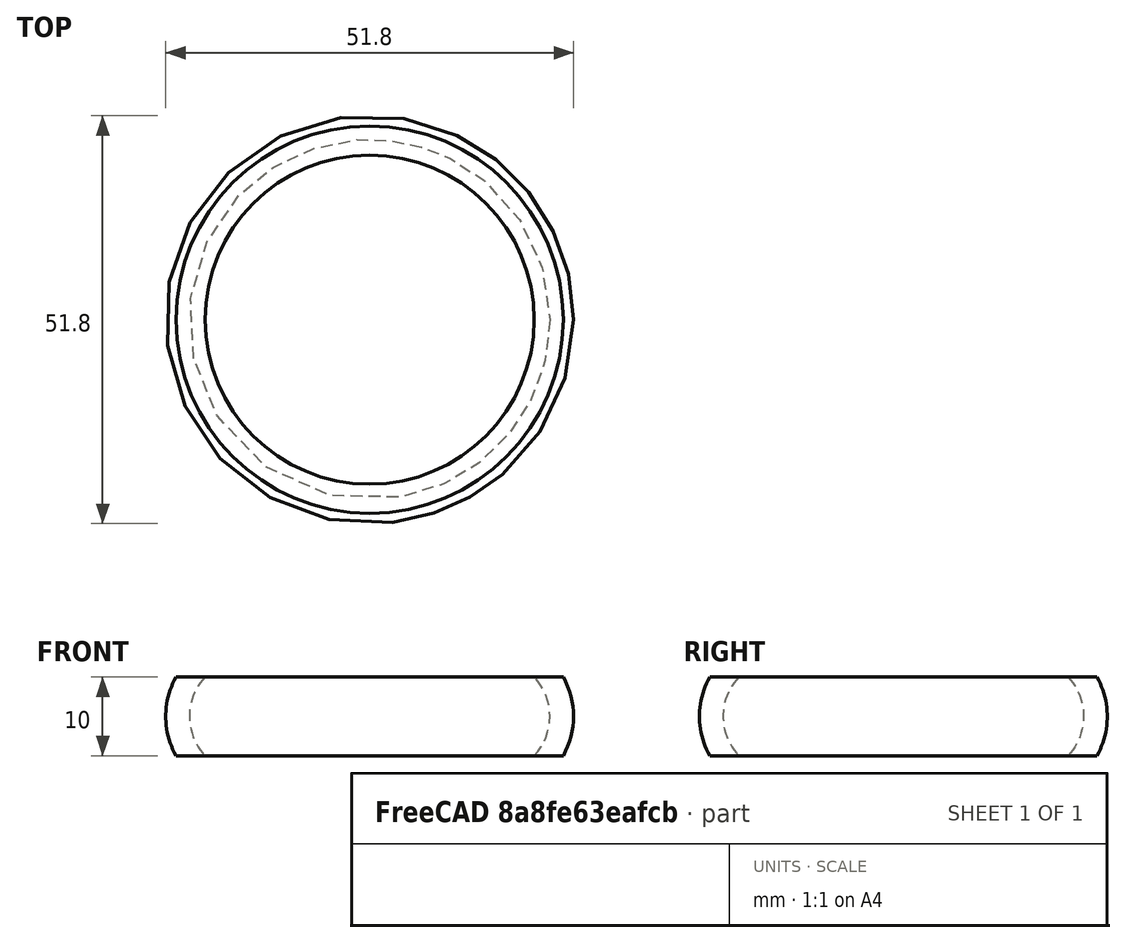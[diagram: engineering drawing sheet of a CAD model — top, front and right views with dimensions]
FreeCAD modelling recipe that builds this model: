
FCSTD DOCUMENT  (FreeCAD 0.20R29410 (Git))
Label: DriveWheelTire
License: All rights reserved
LicenseURL: http://en.wikipedia.org/wiki/All_rights_reserved
objects: App::DocumentObjectGroup×3, PartDesign::CoordinateSystem×1, App::FeaturePython×1, Sketcher::SketchObject×1, PartDesign::Revolution×1, PartDesign::Body×1, App::Part×1
note: 5 computed .brp shape members not serialized (recipe doc carries the construction recipe); baked Part::Feature solids carry a one-line shape summary decoded from their .brp
EXTERNAL_REF file=Params.FCStd obj=Spreadsheet

FEATURE [App::DocumentObjectGroup] Parts
FEATURE [PartDesign::CoordinateSystem] LCS_Origin
  AttacherType = Attacher::AttachEngine3D
  MapMode = 2
  Support = -> [X_Axis]
FEATURE [App::FeaturePython] Variables  # WARN: FeaturePython — macro-defined, semantics opaque (R4)
  Type = App::PropertyContainer
FEATURE [App::DocumentObjectGroup] Constraints
FEATURE [App::DocumentObjectGroup] Configurations
FEATURE [Sketcher::SketchObject] Sketch
  FullyConstrained = true
  MapMode = 5
  Placement = pos=(0,0,0) rot=(1,0,0;1.5708rad)
  Support = -> [XZ_Plane001]
  expr: Constraints[10] = <<Params>>#<<Params>>.DriveWheelTireThickness
  expr: Constraints[14] = <<Params>>#<<Params>>.DriveWheelWidth
  expr: Constraints[15] = <<Params>>#<<Params>>.DriveWheelMajorDiameter / 2 - 0.1
  expr: Constraints[21] = <<Params>>#<<Params>>.DriveWheelCrown
  sketch-geometry (7):
    g0: ArcOfCircle CenterX=15.65 CenterY=0 CenterZ=0 NormalX=0 NormalY=0 NormalZ=1 AngleXU=0 Radius=10.25 StartAngle=5.77361 EndAngle=6.79276
    g1: LineSegment StartX=24.5978 StartY=5 StartZ=0 EndX=20.9 EndY=5 EndZ=0
    g2: LineSegment StartX=24.5978 StartY=-5 StartZ=0 EndX=20.9 EndY=-5 EndZ=0
    g3: ArcOfCircle CenterX=15.65 CenterY=0 CenterZ=0 NormalX=0 NormalY=0 NormalZ=1 AngleXU=0 Radius=7.25 StartAngle=5.52217 EndAngle=7.0442
    g4: LineSegment StartX=22.9 StartY=0 StartZ=0 EndX=25.9 EndY=0 EndZ=0
    g5: LineSegment StartX=20.9 StartY=5 StartZ=0 EndX=20.9 EndY=-5 EndZ=0
    g6: LineSegment StartX=22.9 StartY=0 StartZ=0 EndX=20.9 EndY=0 EndZ=0
  constraints (22):
    c: PointOnObject(g0,g-1)
    c: Coincident(g1,g0)
    c: Horizontal(g1)
    c: Coincident(g2,g0)
    c: Horizontal(g2)
    c: Coincident(g3,g1)
    c: Coincident(g3,g2)
    c: PointOnObject(g4,g3)
    c: PointOnObject(g4,g0)
    c: Horizontal(g4)
    c: DistanceX(g4,g4) = 3
    c: Coincident(g5,g1)
    c: Coincident(g5,g2)
    c: Vertical(g5)
    c: DistanceY(g5,g5) = 10
    c: DistanceX(g-1,g4) = 25.9
    c: Coincident(g3,g0)
    c: Coincident(g6,g4)
    c: PointOnObject(g6,g5)
    c: Horizontal(g6)
    c: PointOnObject(g6,g-1)
    c: DistanceX(g6,g6) = 2
FEATURE [PartDesign::Revolution] Revolution
  Angle = 360
  Axis = (0,-2e-16,1)
  Base = (0,0,0)
  Placement = pos=(0,0,0) rot=(1,0,0;1.5708rad)
  Profile = -> Sketch
  ReferenceAxis = -> Sketch [V_Axis]
  Reversed = true
FEATURE [PartDesign::Body] Body
  Group = -> [Sketch,Revolution]
  Origin = -> Origin001
  Tip = -> Revolution
FEATURE [App::Part] Assembly
  AssemblyType = Part::Link
  Group = -> [LCS_Origin,Variables,Constraints,Configurations,Body]
  Origin = -> Origin
  Type = Assembly
